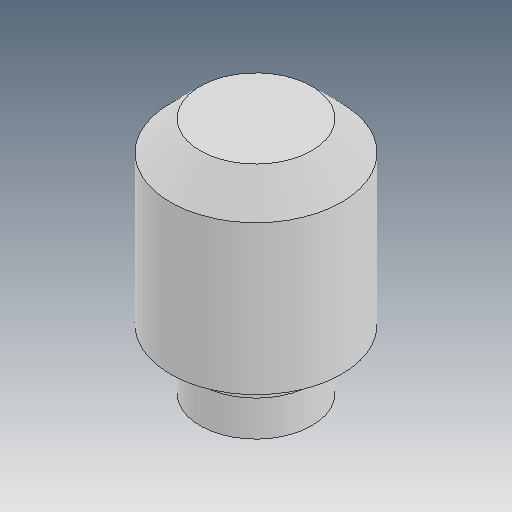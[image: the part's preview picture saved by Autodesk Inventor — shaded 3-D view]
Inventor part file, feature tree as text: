
AUTODESK INVENTOR PART (.ipt)
format: ipt  version: 2020 (Build 240168000, 168)  size: 129,024 bytes
history: native  units: mm
features: revolve x1, sketch x1
ambient origin geometry x8: Origin, YZ Plane, XZ Plane, XY Plane, X Axis, Y Axis, Z Axis, Center Point
bodies: Solid1 (feature_tree)
feature tree (2):
  revolve  "Revolution1"  [1 undecoded]
  sketch  "Sketch1"  dims[d0=3.75mm d1=4.0mm d2=2.0mm d3=12.0mm d4=1.0mm d5=1.0mm d6=2.0mm d7=2.0mm d8=90.0deg]
note: 1 required parameter value undecoded (feature->parameter linkage not recoverable at this tier; creation-order binding heuristic only, values carry confidence <= 0.55)
